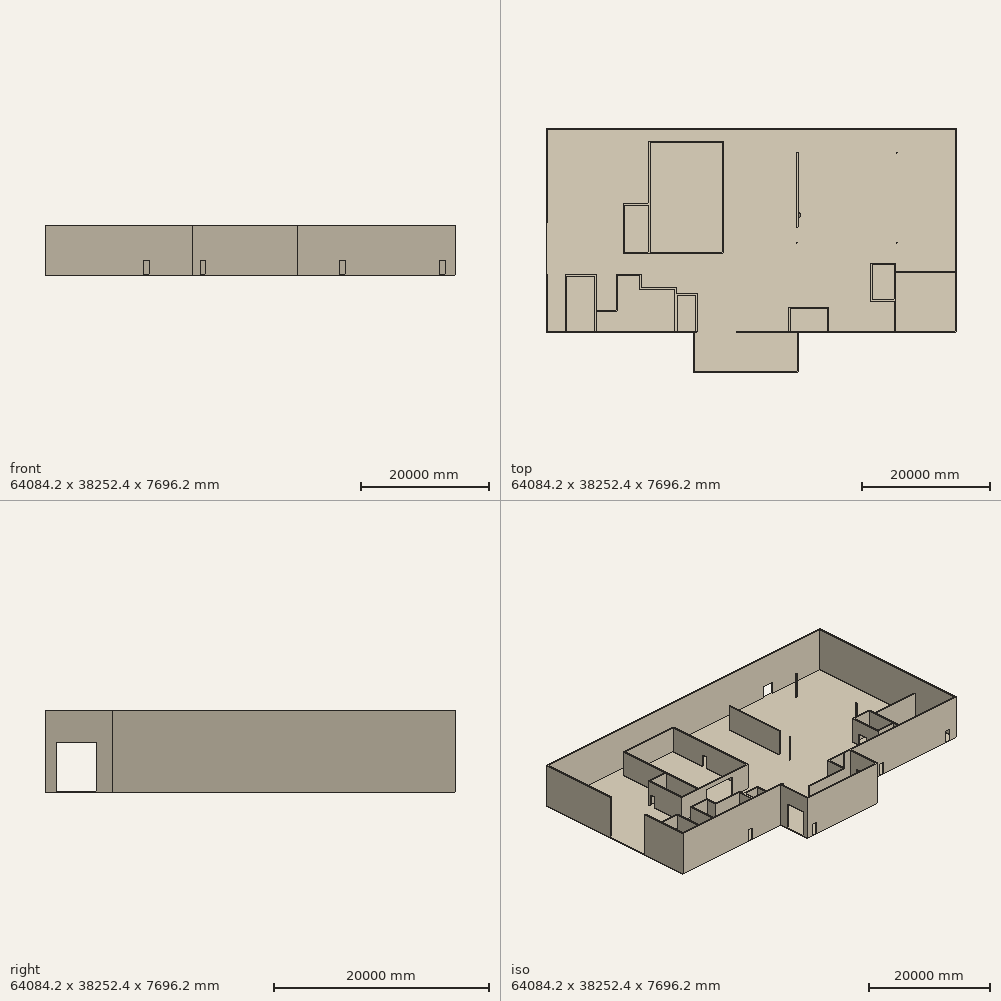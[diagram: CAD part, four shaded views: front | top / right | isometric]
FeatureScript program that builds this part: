
annotation { "Feature Type Name" : "Feature", "Feature Type Description" : "" }
export const myFeature = defineFeature(function(context is Context, id is Id, definition is map)
    precondition{}
    {
        {
            var Q0;
            Q0=qCreatedBy(makeId("Top.planeOp"),FACE);
            var sketch = newSketch(context, id + "F0", { "sketchPlane" : qUnion([Q0])});
            skLineSegment(sketch, "E0.bottom", {"start": v(-27660.6, 28059.69) * mm, "end": v(36423.6, 28059.69) * mm});
            skLineSegment(sketch, "E0.top", {"start": v(-27660.6, -3944.31) * mm, "end": v(36423.6, -3944.31) * mm});
            skLineSegment(sketch, "E0.left", {"start": v(-27660.6, 28059.69) * mm, "end": v(-27660.6, -3944.31) * mm});
            skLineSegment(sketch, "E0.right", {"start": v(36423.6, 28059.69) * mm, "end": v(36423.6, -3944.31) * mm});
            skLineSegment(sketch, "E1.bottom", {"start": v(-11658.6, 26002.29) * mm, "end": v(0, 26002.29) * mm});
            skLineSegment(sketch, "E1.top", {"start": v(-11658.6, 8400.09) * mm, "end": v(0, 8400.09) * mm});
            skLineSegment(sketch, "E1.left", {"start": v(-11658.6, 26002.29) * mm, "end": v(-11658.6, 8400.09) * mm});
            skLineSegment(sketch, "E1.right", {"start": v(0, 26002.29) * mm, "end": v(0, 8400.09) * mm});
            skLineSegment(sketch, "E2.bottom", {"start": v(-15621, 16248.69) * mm, "end": v(-11658.6, 16248.69) * mm});
            skLineSegment(sketch, "E2.top", {"start": v(-15621, 8400.09) * mm, "end": v(-11658.6, 8400.09) * mm});
            skLineSegment(sketch, "E2.left", {"start": v(-15621, 16248.69) * mm, "end": v(-15621, 8400.09) * mm});
            skLineSegment(sketch, "E2.right", {"start": v(-11658.6, 16248.69) * mm, "end": v(-11658.6, 8400.09) * mm});
            skLineSegment(sketch, "E3.bottom", {"start": v(-24765, 5123.49) * mm, "end": v(-19888.2, 5123.49) * mm});
            skLineSegment(sketch, "E3.left", {"start": v(-24765, 5123.49) * mm, "end": v(-24765, -3715.71) * mm});
            skLineSegment(sketch, "E3.right", {"start": v(-19888.2, 5123.49) * mm, "end": v(-19888.2, -3715.71) * mm});
            skLineSegment(sketch, "E4", {"start": v(-19888.2, -439.11) * mm, "end": v(-16764, -439.11) * mm});
            skLineSegment(sketch, "E5", {"start": v(-16764, -439.11) * mm, "end": v(-16764, 5199.69) * mm});
            skLineSegment(sketch, "E6", {"start": v(-16764, 5199.69) * mm, "end": v(-12877.8, 5199.69) * mm});
            skLineSegment(sketch, "E7", {"start": v(-12877.8, 5199.69) * mm, "end": v(-12877.8, 3142.29) * mm});
            skLineSegment(sketch, "E8", {"start": v(-12877.8, 3142.29) * mm, "end": v(-7391.4, 3142.29) * mm});
            skLineSegment(sketch, "E9.bottom", {"start": v(-4114.8, 2151.69) * mm, "end": v(-7391.4, 2151.69) * mm});
            skLineSegment(sketch, "E9.top", {"start": v(-4114.8, -3944.31) * mm, "end": v(-4724.4, -3944.31) * mm});
            skLineSegment(sketch, "E9.left", {"start": v(-4114.8, 2151.69) * mm, "end": v(-4114.8, -3715.71) * mm});
            skLineSegment(sketch, "E10.bottom", {"start": v(10210.8, 94.29) * mm, "end": v(16459.2, 94.29) * mm});
            skLineSegment(sketch, "E10.top", {"start": v(10210.8, -3715.71) * mm, "end": v(16459.2, -3715.71) * mm});
            skLineSegment(sketch, "E10.left", {"start": v(10210.8, 94.29) * mm, "end": v(10210.8, -3715.71) * mm});
            skLineSegment(sketch, "E10.right", {"start": v(16459.2, 94.29) * mm, "end": v(16459.2, -3715.71) * mm});
            skLineSegment(sketch, "E11.bottom", {"start": v(23012.4, 6952.29) * mm, "end": v(26898.6, 6952.29) * mm});
            skLineSegment(sketch, "E11.top", {"start": v(23012.4, 1008.69) * mm, "end": v(26670, 1008.69) * mm});
            skLineSegment(sketch, "E11.left", {"start": v(23012.4, 6952.29) * mm, "end": v(23012.4, 1008.69) * mm});
            skLineSegment(sketch, "E12.bottom", {"start": v(26898.6, 5428.29) * mm, "end": v(36195, 5428.29) * mm});
            skLineSegment(sketch, "E12.left", {"start": v(26898.6, 5428.29) * mm, "end": v(26898.6, -3715.71) * mm});
            skLineSegment(sketch, "E13", {"start": v(11430, 24325.89) * mm, "end": v(11430, 12591.09) * mm});
            skLineSegment(sketch, "E14", {"start": v(-24765, 5123.49) * mm, "end": v(-27432, 5123.49) * mm, "construction": true});
            skLineSegment(sketch, "E15", {"start": v(-24765, 4056.69) * mm, "end": v(-24536.4, 4056.69) * mm});
            skLineSegment(sketch, "E16", {"start": v(-24765, 3142.29) * mm, "end": v(-24536.4, 3142.29) * mm});
            skLineSegment(sketch, "E17", {"start": v(-21259.8, 5123.49) * mm, "end": v(-21259.8, 4894.89) * mm});
            skLineSegment(sketch, "E18", {"start": v(-20345.4, 5123.49) * mm, "end": v(-20345.4, 4894.89) * mm});
            skLineSegment(sketch, "E19", {"start": v(-12725.4, 3142.29) * mm, "end": v(-12725.4, 2913.69) * mm});
            skLineSegment(sketch, "E20", {"start": v(-10744.2, 3142.29) * mm, "end": v(-10744.2, 2913.69) * mm});
            skLineSegment(sketch, "E21", {"start": v(-4343.4, -2039.31) * mm, "end": v(-4114.8, -2039.31) * mm});
            skLineSegment(sketch, "E22", {"start": v(-4343.4, -2953.71) * mm, "end": v(-4114.8, -2953.71) * mm});
            skLineSegment(sketch, "E23", {"start": v(10591.8, 94.29) * mm, "end": v(10591.8, -134.31) * mm});
            skLineSegment(sketch, "E24", {"start": v(11506.2, 94.29) * mm, "end": v(11506.2, -134.31) * mm});
            skLineSegment(sketch, "E25", {"start": v(18288, -3715.71) * mm, "end": v(18288, -3944.31) * mm});
            skLineSegment(sketch, "E26", {"start": v(19202.4, -3715.71) * mm, "end": v(19202.4, -3944.31) * mm});
            skLineSegment(sketch, "E27.bottom", {"start": v(-4724.4, -3944.31) * mm, "end": v(11734.8, -3944.31) * mm});
            skLineSegment(sketch, "E27.top", {"start": v(-4724.4, -10192.71) * mm, "end": v(11734.8, -10192.71) * mm});
            skLineSegment(sketch, "E27.left", {"start": v(-4724.4, -3944.31) * mm, "end": v(-4724.4, -10192.71) * mm});
            skLineSegment(sketch, "E27.right", {"start": v(11734.8, -3944.31) * mm, "end": v(11734.8, -10192.71) * mm});
            skLineSegment(sketch, "E28", {"start": v(23241, 5580.69) * mm, "end": v(23012.4, 5580.69) * mm});
            skLineSegment(sketch, "E29", {"start": v(23241, 3675.69) * mm, "end": v(23012.4, 3675.69) * mm});
            skLineSegment(sketch, "E30", {"start": v(27432, 5656.89) * mm, "end": v(27432, 5428.29) * mm});
            skLineSegment(sketch, "E31", {"start": v(29413.2, 5656.89) * mm, "end": v(29413.2, 5428.29) * mm});
            skLineSegment(sketch, "E32", {"start": v(23012.4, 28059.69) * mm, "end": v(23012.4, 27831.09) * mm});
            skLineSegment(sketch, "E33", {"start": v(25146, 27831.09) * mm, "end": v(25146, 28059.69) * mm});
            skLineSegment(sketch, "E34", {"start": v(-914.4, 27831.09) * mm, "end": v(-914.4, 28059.69) * mm});
            skLineSegment(sketch, "E35", {"start": v(1600.2, 27831.09) * mm, "end": v(1600.2, 28059.69) * mm});
            skLineSegment(sketch, "E36", {"start": v(-26136.6, 27831.09) * mm, "end": v(-26136.6, 28059.69) * mm});
            skLineSegment(sketch, "E37", {"start": v(-24003, 27831.09) * mm, "end": v(-24003, 28059.69) * mm});
            skLineSegment(sketch, "E38", {"start": v(-15621, 15791.49) * mm, "end": v(-15392.4, 15791.49) * mm});
            skLineSegment(sketch, "E39", {"start": v(-15621, 14877.09) * mm, "end": v(-15392.4, 14877.09) * mm});
            skLineSegment(sketch, "E40", {"start": v(-228.6, 18839.49) * mm, "end": v(0, 18839.49) * mm});
            skLineSegment(sketch, "E41", {"start": v(-228.6, 17925.09) * mm, "end": v(0, 17925.09) * mm});
            skLineSegment(sketch, "E42", {"start": v(-12344.4, -3715.71) * mm, "end": v(-12344.4, -3944.31) * mm});
            skLineSegment(sketch, "E43", {"start": v(-11430, -3715.71) * mm, "end": v(-11430, -3944.31) * mm});
            skLineSegment(sketch, "E44", {"start": v(33909, -3715.71) * mm, "end": v(33909, -3944.31) * mm});
            skLineSegment(sketch, "E45", {"start": v(34899.6, -3715.71) * mm, "end": v(34899.6, -3944.31) * mm});
            skLineSegment(sketch, "E46.0", {"start": v(-27432, 27831.09) * mm, "end": v(36195, 27831.09) * mm});
            skLineSegment(sketch, "E46.1", {"start": v(-27432, 27831.09) * mm, "end": v(-27432, -3715.71) * mm});
            skLineSegment(sketch, "E46.2", {"start": v(-27432, -3715.71) * mm, "end": v(36195, -3715.71) * mm});
            skLineSegment(sketch, "E46.3", {"start": v(36195, 27831.09) * mm, "end": v(36195, -3715.71) * mm});
            skLineSegment(sketch, "E47.0", {"start": v(26670, 5656.89) * mm, "end": v(36195, 5656.89) * mm});
            skLineSegment(sketch, "E47.1", {"start": v(26670, 5656.89) * mm, "end": v(26670, -3715.71) * mm});
            skLineSegment(sketch, "E48", {"start": v(26898.6, 5656.89) * mm, "end": v(26898.6, 6952.29) * mm});
            skLineSegment(sketch, "E49.0", {"start": v(23241, 1237.29) * mm, "end": v(26670, 1237.29) * mm});
            skLineSegment(sketch, "E49.1", {"start": v(23241, 6723.69) * mm, "end": v(23241, 1237.29) * mm});
            skLineSegment(sketch, "E49.2", {"start": v(23241, 6723.69) * mm, "end": v(26670, 6723.69) * mm});
            skLineSegment(sketch, "E49.3", {"start": v(26670, 5656.89) * mm, "end": v(26670, 6723.69) * mm});
            skLineSegment(sketch, "E50.0", {"start": v(10439.4, -134.31) * mm, "end": v(10439.4, -3715.71) * mm});
            skLineSegment(sketch, "E50.1", {"start": v(10439.4, -134.31) * mm, "end": v(16230.6, -134.31) * mm});
            skLineSegment(sketch, "E50.2", {"start": v(16230.6, -134.31) * mm, "end": v(16230.6, -3715.71) * mm});
            skLineSegment(sketch, "E51.0", {"start": v(11506.2, -3944.31) * mm, "end": v(11506.2, -9964.11) * mm});
            skLineSegment(sketch, "E51.1", {"start": v(-4495.8, -9964.11) * mm, "end": v(11506.2, -9964.11) * mm});
            skLineSegment(sketch, "E51.2", {"start": v(-4495.8, -3944.31) * mm, "end": v(-4495.8, -9964.11) * mm});
            skLineSegment(sketch, "E52", {"start": v(-7391.4, -3715.71) * mm, "end": v(-7391.4, 3142.29) * mm});
            skLineSegment(sketch, "E53.0", {"start": v(-4343.4, 1923.09) * mm, "end": v(-7162.8, 1923.09) * mm});
            skLineSegment(sketch, "E53.1", {"start": v(-4343.4, 1923.09) * mm, "end": v(-4343.4, -3715.71) * mm});
            skLineSegment(sketch, "E54", {"start": v(-7162.8, 1923.09) * mm, "end": v(-7162.8, -3715.71) * mm});
            skLineSegment(sketch, "E55.0", {"start": v(-7620, -3715.71) * mm, "end": v(-7620, 2913.69) * mm});
            skLineSegment(sketch, "E55.1", {"start": v(-13106.4, 2913.69) * mm, "end": v(-7620, 2913.69) * mm});
            skLineSegment(sketch, "E55.2", {"start": v(-19888.2, -667.71) * mm, "end": v(-16535.4, -667.71) * mm});
            skLineSegment(sketch, "E55.3", {"start": v(-16535.4, -667.71) * mm, "end": v(-16535.4, 4971.09) * mm});
            skLineSegment(sketch, "E55.4", {"start": v(-16535.4, 4971.09) * mm, "end": v(-13106.4, 4971.09) * mm});
            skLineSegment(sketch, "E55.5", {"start": v(-13106.4, 4971.09) * mm, "end": v(-13106.4, 2913.69) * mm});
            skLineSegment(sketch, "E56.0", {"start": v(-24536.4, 4894.89) * mm, "end": v(-24536.4, -3715.71) * mm});
            skLineSegment(sketch, "E56.1", {"start": v(-24536.4, 4894.89) * mm, "end": v(-20116.8, 4894.89) * mm});
            skLineSegment(sketch, "E56.2", {"start": v(-20116.8, 4894.89) * mm, "end": v(-20116.8, -3715.71) * mm});
            skLineSegment(sketch, "E57.0", {"start": v(-15392.4, 16020.09) * mm, "end": v(-11658.6, 16020.09) * mm});
            skLineSegment(sketch, "E57.1", {"start": v(-15392.4, 16020.09) * mm, "end": v(-15392.4, 8628.69) * mm});
            skLineSegment(sketch, "E57.2", {"start": v(-15392.4, 8628.69) * mm, "end": v(-11658.6, 8628.69) * mm});
            skLineSegment(sketch, "E58.0", {"start": v(-11430, 25773.69) * mm, "end": v(-11430, 8628.69) * mm});
            skLineSegment(sketch, "E58.1", {"start": v(-11430, 25773.69) * mm, "end": v(-228.6, 25773.69) * mm});
            skLineSegment(sketch, "E58.2", {"start": v(-228.6, 25773.69) * mm, "end": v(-228.6, 8628.69) * mm});
            skLineSegment(sketch, "E58.3", {"start": v(-11430, 8628.69) * mm, "end": v(-228.6, 8628.69) * mm});
            skLineSegment(sketch, "E59", {"start": v(11430, 24325.89) * mm, "end": v(11658.6, 24325.89) * mm});
            skLineSegment(sketch, "E60", {"start": v(11658.6, 24325.89) * mm, "end": v(11658.6, 12591.09) * mm});
            skLineSegment(sketch, "E61", {"start": v(11658.6, 12591.09) * mm, "end": v(11430, 12591.09) * mm});
            skPoint(sketch, "E62", {"position": v(-27432, 13124.49) * mm});
            skPoint(sketch, "E63", {"position": v(-27660.6, 13124.49) * mm});
            skLineSegment(sketch, "E64", {"start": v(-27660.6, 5123.49) * mm, "end": v(-27660.6, -3944.31) * mm});
            skLineSegment(sketch, "E65", {"start": v(-27432, 5123.49) * mm, "end": v(-27432, -3715.71) * mm});
            skLineSegment(sketch, "E66", {"start": v(-27660.6, 13124.49) * mm, "end": v(-27660.6, 28059.69) * mm});
            skLineSegment(sketch, "E67", {"start": v(-27432, 27831.09) * mm, "end": v(-27432, 13124.49) * mm});
            skLineSegment(sketch, "E68", {"start": v(-27432, 5123.49) * mm, "end": v(-27660.6, 5123.49) * mm});
            skLineSegment(sketch, "E69", {"start": v(-27432, 13124.49) * mm, "end": v(-27660.6, 13124.49) * mm});
            skLineSegment(sketch, "E70.bottom", {"start": v(11353.8, 10152.69) * mm, "end": v(11506.2, 10152.69) * mm});
            skLineSegment(sketch, "E70.top", {"start": v(11353.8, 10000.29) * mm, "end": v(11506.2, 10000.29) * mm});
            skLineSegment(sketch, "E70.left", {"start": v(11353.8, 10152.69) * mm, "end": v(11353.8, 10000.29) * mm});
            skLineSegment(sketch, "E70.right", {"start": v(11506.2, 10152.69) * mm, "end": v(11506.2, 10000.29) * mm});
            skLineSegment(sketch, "E71", {"start": v(10210.8, -3715.71) * mm, "end": v(10210.8, -3944.31) * mm});
            skLineSegment(sketch, "E72", {"start": v(-4114.8, -3715.71) * mm, "end": v(-4114.8, -3944.31) * mm});
            skLineSegment(sketch, "E73", {"start": v(-4724.4, -5468.31) * mm, "end": v(-4495.8, -5468.31) * mm});
            skLineSegment(sketch, "E74", {"start": v(-4724.4, -9125.91) * mm, "end": v(-4495.8, -9125.91) * mm});
            skLineSegment(sketch, "E75", {"start": v(11506.2, -5468.31) * mm, "end": v(11734.8, -5468.31) * mm});
            skLineSegment(sketch, "E76", {"start": v(11506.2, -9125.91) * mm, "end": v(11734.8, -9125.91) * mm});
            skLineSegment(sketch, "E77", {"start": v(-3505.2, -9964.11) * mm, "end": v(-3505.2, -10192.71) * mm});
            skLineSegment(sketch, "E78", {"start": v(-2590.8, -9964.11) * mm, "end": v(-2590.8, -10192.71) * mm});
            skLineSegment(sketch, "E79.bottom", {"start": v(26974.8, 24249.69) * mm, "end": v(27127.2, 24249.69) * mm});
            skLineSegment(sketch, "E79.top", {"start": v(26974.8, 24097.29) * mm, "end": v(27127.2, 24097.29) * mm});
            skLineSegment(sketch, "E79.left", {"start": v(26974.8, 24249.69) * mm, "end": v(26974.8, 24097.29) * mm});
            skLineSegment(sketch, "E79.right", {"start": v(27127.2, 24249.69) * mm, "end": v(27127.2, 24097.29) * mm});
            skLineSegment(sketch, "E80.bottom", {"start": v(26974.8, 10228.89) * mm, "end": v(27127.2, 10228.89) * mm});
            skLineSegment(sketch, "E80.top", {"start": v(26974.8, 10076.49) * mm, "end": v(27127.2, 10076.49) * mm});
            skLineSegment(sketch, "E80.left", {"start": v(26974.8, 10228.89) * mm, "end": v(26974.8, 10076.49) * mm});
            skLineSegment(sketch, "E80.right", {"start": v(27127.2, 10228.89) * mm, "end": v(27127.2, 10076.49) * mm});
            skLineSegment(sketch, "E81.bottom", {"start": v(1981.2, -3715.71) * mm, "end": v(9906, -3715.71) * mm});
            skLineSegment(sketch, "E81.top", {"start": v(1981.2, 1465.89) * mm, "end": v(9906, 1465.89) * mm});
            skLineSegment(sketch, "E81.left", {"start": v(1981.2, -3715.71) * mm, "end": v(1981.2, 1465.89) * mm});
            skLineSegment(sketch, "E81.right", {"start": v(9906, -3715.71) * mm, "end": v(9906, 1465.89) * mm});
            skLineSegment(sketch, "E82.0", {"start": v(9677.4, -3715.71) * mm, "end": v(9677.4, 1237.29) * mm});
            skLineSegment(sketch, "E82.1", {"start": v(2209.8, 1237.29) * mm, "end": v(9677.4, 1237.29) * mm});
            skLineSegment(sketch, "E82.2", {"start": v(2209.8, -3715.71) * mm, "end": v(2209.8, 1237.29) * mm});
            skLineSegment(sketch, "E83", {"start": v(1981.2, 1084.89) * mm, "end": v(2209.8, 1084.89) * mm});
            skLineSegment(sketch, "E84", {"start": v(1981.2, 170.49) * mm, "end": v(2209.8, 170.49) * mm});
            skLineSegment(sketch, "E85", {"start": v(9677.4, 1084.89) * mm, "end": v(9906, 1084.89) * mm});
            skLineSegment(sketch, "E86", {"start": v(9677.4, 170.49) * mm, "end": v(9906, 170.49) * mm});
            skLineSegment(sketch, "E87", {"start": v(1981.2, -3715.71) * mm, "end": v(1981.2, -3944.31) * mm});
            skSolve(sketch);
        }
        {
            var Q0;
            Q0=qCreatedBy(makeId("Top.planeOp"),FACE);
            var sketch = newSketch(context, id + "F1", { "sketchPlane" : qUnion([Q0])});
            skLineSegment(sketch, "E88.0", {"start": v(-27660.6, 28059.69) * mm, "end": v(36423.6, 28059.69) * mm});
            skLineSegment(sketch, "E89.0", {"start": v(-27660.6, 28059.69) * mm, "end": v(-27660.6, -3944.31) * mm});
            skLineSegment(sketch, "E90.0", {"start": v(-27660.6, -3944.31) * mm, "end": v(36423.6, -3944.31) * mm});
            skLineSegment(sketch, "E91.0", {"start": v(36423.6, 28059.69) * mm, "end": v(36423.6, -3944.31) * mm});
            skPoint(sketch, "E92.0", {"position": v(-4724.4, -7068.51) * mm});
            skLineSegment(sketch, "E93.0", {"start": v(-4724.4, -3944.31) * mm, "end": v(-4724.4, -10192.71) * mm});
            skLineSegment(sketch, "E94.0", {"start": v(-4724.4, -10192.71) * mm, "end": v(11734.8, -10192.71) * mm});
            skLineSegment(sketch, "E95.0", {"start": v(11734.8, -3944.31) * mm, "end": v(11734.8, -10192.71) * mm});
            skSolve(sketch);
        }
        {
            var Q0;
            Q0 = qSketchRegion(id + "F1", true);
            extrude(context, id + "F2", {"entities" : qUnion([Q0]), "oppositeDirection" : true, "depth" : 76.2 * mm, "offsetDistance" : 30.48 * mm});
        }
        {
            var Q0;
            {var subQ1=sQuery(id+"F0.wireOp",EDGE,"E36");Q0=makeQuery(id+"F0.imprint","IMPRINT",FACE,{"disambiguationData":[TD([[makeQuery(id+"F0.imprint","IMPRINT",EDGE,{"derivedFrom":subQ1}),1.0]])]});}
            var Q1;
            {var subQ2=sQuery(id+"F0.wireOp",EDGE,"E34");Q1=makeQuery(id+"F0.imprint","IMPRINT",FACE,{"disambiguationData":[TD([[makeQuery(id+"F0.imprint","IMPRINT",EDGE,{"derivedFrom":subQ2}),1.0]])]});}
            var Q2;
            {var subQ0=sQuery(id+"F0.wireOp",EDGE,"E32");Q2=makeQuery(id+"F0.imprint","IMPRINT",FACE,{"disambiguationData":[TD([[makeQuery(id+"F0.imprint","IMPRINT",EDGE,{"derivedFrom":subQ0}),-1.0]])]});}
            var Q3;
            {var subQ0=sQuery(id+"F0.wireOp",EDGE,"E0.right");Q3=makeQuery(id+"F0.imprint","IMPRINT",FACE,{"disambiguationData":[TD([[makeQuery(id+"F0.imprint","IMPRINT",EDGE,{"derivedFrom":subQ0}),-1.0]])]});}
            var Q4;
            {var subQ1=sQuery(id+"F0.wireOp",EDGE,"E26");Q4=makeQuery(id+"F0.imprint","IMPRINT",FACE,{"disambiguationData":[TD([[makeQuery(id+"F0.imprint","IMPRINT",EDGE,{"derivedFrom":subQ1}),1.0]])]});}
            var Q5;
            {var subQ9=sQuery(id+"F0.wireOp",EDGE,"E25");Q5=makeQuery(id+"F0.imprint","IMPRINT",FACE,{"disambiguationData":[TD([[makeQuery(id+"F0.imprint","IMPRINT",EDGE,{"derivedFrom":subQ9}),-1.0]])]});}
            var Q6;
            {var subQ5=sQuery(id+"F0.wireOp",EDGE,"E75");Q6=makeQuery(id+"F0.imprint","IMPRINT",FACE,{"disambiguationData":[TD([[makeQuery(id+"F0.imprint","IMPRINT",EDGE,{"derivedFrom":subQ5}),1.0]])]});}
            var Q7;
            {var subQ3=sQuery(id+"F0.wireOp",EDGE,"E76");Q7=makeQuery(id+"F0.imprint","IMPRINT",FACE,{"disambiguationData":[TD([[makeQuery(id+"F0.imprint","IMPRINT",EDGE,{"derivedFrom":subQ3}),-1.0]])]});}
            var Q8;
            {var subQ3=sQuery(id+"F0.wireOp",EDGE,"E74");Q8=makeQuery(id+"F0.imprint","IMPRINT",FACE,{"disambiguationData":[TD([[makeQuery(id+"F0.imprint","IMPRINT",EDGE,{"derivedFrom":subQ3}),-1.0]])]});}
            var Q9;
            {var subQ5=sQuery(id+"F0.wireOp",EDGE,"E73");Q9=makeQuery(id+"F0.imprint","IMPRINT",FACE,{"disambiguationData":[TD([[makeQuery(id+"F0.imprint","IMPRINT",EDGE,{"derivedFrom":subQ5}),1.0]])]});}
            var Q10;
            {var subQ3=sQuery(id+"F0.wireOp",EDGE,"E43");Q10=makeQuery(id+"F0.imprint","IMPRINT",FACE,{"disambiguationData":[TD([[makeQuery(id+"F0.imprint","IMPRINT",EDGE,{"derivedFrom":subQ3}),1.0]])]});}
            var Q11;
            {var subQ4=sQuery(id+"F0.wireOp",EDGE,"E42");Q11=makeQuery(id+"F0.imprint","IMPRINT",FACE,{"disambiguationData":[TD([[makeQuery(id+"F0.imprint","IMPRINT",EDGE,{"derivedFrom":subQ4}),-1.0]])]});}
            var Q12;
            {var subQ0=sQuery(id+"F0.wireOp",EDGE,"E42");Q12=makeQuery(id+"F0.imprint","IMPRINT",FACE,{"disambiguationData":[TD([[makeQuery(id+"F0.imprint","IMPRINT",EDGE,{"derivedFrom":subQ0}),1.0]])]});}
            var Q13;
            {var subQ0=sQuery(id+"F0.wireOp",EDGE,"E73");Q13=makeQuery(id+"F0.imprint","IMPRINT",FACE,{"disambiguationData":[TD([[makeQuery(id+"F0.imprint","IMPRINT",EDGE,{"derivedFrom":subQ0}),-1.0]])]});}
            var Q14;
            {var subQ2=sQuery(id+"F0.wireOp",EDGE,"E77");Q14=makeQuery(id+"F0.imprint","IMPRINT",FACE,{"disambiguationData":[TD([[makeQuery(id+"F0.imprint","IMPRINT",EDGE,{"derivedFrom":subQ2}),1.0]])]});}
            var Q15;
            {var subQ0=sQuery(id+"F0.wireOp",EDGE,"E75");Q15=makeQuery(id+"F0.imprint","IMPRINT",FACE,{"disambiguationData":[TD([[makeQuery(id+"F0.imprint","IMPRINT",EDGE,{"derivedFrom":subQ0}),-1.0]])]});}
            var Q16;
            {var subQ0=sQuery(id+"F0.wireOp",EDGE,"E25");Q16=makeQuery(id+"F0.imprint","IMPRINT",FACE,{"disambiguationData":[TD([[makeQuery(id+"F0.imprint","IMPRINT",EDGE,{"derivedFrom":subQ0}),1.0]])]});}
            var Q17;
            {var subQ0=sQuery(id+"F0.wireOp",EDGE,"E44");Q17=makeQuery(id+"F0.imprint","IMPRINT",FACE,{"disambiguationData":[TD([[makeQuery(id+"F0.imprint","IMPRINT",EDGE,{"derivedFrom":subQ0}),1.0]])]});}
            var Q18;
            {var subQ0=sQuery(id+"F0.wireOp",EDGE,"E32");Q18=makeQuery(id+"F0.imprint","IMPRINT",FACE,{"disambiguationData":[TD([[makeQuery(id+"F0.imprint","IMPRINT",EDGE,{"derivedFrom":subQ0}),1.0]])]});}
            var Q19;
            {var subQ0=sQuery(id+"F0.wireOp",EDGE,"E34");Q19=makeQuery(id+"F0.imprint","IMPRINT",FACE,{"disambiguationData":[TD([[makeQuery(id+"F0.imprint","IMPRINT",EDGE,{"derivedFrom":subQ0}),-1.0]])]});}
            var Q20;
            {var subQ2=sQuery(id+"F0.wireOp",EDGE,"E36");Q20=makeQuery(id+"F0.imprint","IMPRINT",FACE,{"disambiguationData":[TD([[makeQuery(id+"F0.imprint","IMPRINT",EDGE,{"derivedFrom":subQ2}),-1.0]])]});}
            extrude(context, id + "F3", {"entities" : qUnion([Q0, Q1, Q2, Q3, Q4, Q5, Q6, Q7, Q8, Q9, Q10, Q11, Q12, Q13, Q14, Q15, Q16, Q17, Q18, Q19, Q20]), "operationType" : NewBodyOperationType.ADD, "depth" : 7620 * mm, "offsetDistance" : 30.48 * mm});
        }
        {
            var Q0;
            {var subQ0=sQuery(id+"F0.wireOp",EDGE,"E42");Q0=makeQuery(id+"F0.imprint","IMPRINT",FACE,{"disambiguationData":[TD([[makeQuery(id+"F0.imprint","IMPRINT",EDGE,{"derivedFrom":subQ0}),1.0]])]});}
            var Q1;
            {var subQ2=sQuery(id+"F0.wireOp",EDGE,"E77");Q1=makeQuery(id+"F0.imprint","IMPRINT",FACE,{"disambiguationData":[TD([[makeQuery(id+"F0.imprint","IMPRINT",EDGE,{"derivedFrom":subQ2}),1.0]])]});}
            var Q2;
            {var subQ0=sQuery(id+"F0.wireOp",EDGE,"E25");Q2=makeQuery(id+"F0.imprint","IMPRINT",FACE,{"disambiguationData":[TD([[makeQuery(id+"F0.imprint","IMPRINT",EDGE,{"derivedFrom":subQ0}),1.0]])]});}
            var Q3;
            {var subQ0=sQuery(id+"F0.wireOp",EDGE,"E44");Q3=makeQuery(id+"F0.imprint","IMPRINT",FACE,{"disambiguationData":[TD([[makeQuery(id+"F0.imprint","IMPRINT",EDGE,{"derivedFrom":subQ0}),1.0]])]});}
            var Q4;
            {var subQ0=sQuery(id+"F0.wireOp",EDGE,"E32");Q4=makeQuery(id+"F0.imprint","IMPRINT",FACE,{"disambiguationData":[TD([[makeQuery(id+"F0.imprint","IMPRINT",EDGE,{"derivedFrom":subQ0}),1.0]])]});}
            var Q5;
            {var subQ0=sQuery(id+"F0.wireOp",EDGE,"E34");Q5=makeQuery(id+"F0.imprint","IMPRINT",FACE,{"disambiguationData":[TD([[makeQuery(id+"F0.imprint","IMPRINT",EDGE,{"derivedFrom":subQ0}),-1.0]])]});}
            var Q6;
            {var subQ2=sQuery(id+"F0.wireOp",EDGE,"E36");Q6=makeQuery(id+"F0.imprint","IMPRINT",FACE,{"disambiguationData":[TD([[makeQuery(id+"F0.imprint","IMPRINT",EDGE,{"derivedFrom":subQ2}),-1.0]])]});}
            extrude(context, id + "F4", {"entities" : qUnion([Q0, Q1, Q2, Q3, Q4, Q5, Q6]), "operationType" : NewBodyOperationType.REMOVE, "depth" : 2133.6 * mm, "offsetDistance" : 30.48 * mm});
        }
        {
            var Q0;
            {var subQ0=sQuery(id+"F0.wireOp",EDGE,"E73");Q0=makeQuery(id+"F0.imprint","IMPRINT",FACE,{"disambiguationData":[TD([[makeQuery(id+"F0.imprint","IMPRINT",EDGE,{"derivedFrom":subQ0}),-1.0]])]});}
            var Q1;
            {var subQ0=sQuery(id+"F0.wireOp",EDGE,"E75");Q1=makeQuery(id+"F0.imprint","IMPRINT",FACE,{"disambiguationData":[TD([[makeQuery(id+"F0.imprint","IMPRINT",EDGE,{"derivedFrom":subQ0}),-1.0]])]});}
            extrude(context, id + "F5", {"entities" : qUnion([Q0, Q1]), "operationType" : NewBodyOperationType.REMOVE, "depth" : 4572 * mm, "offsetDistance" : 30.48 * mm});
        }
        {
            var Q0;
            {var subQ0=sQuery(id+"F0.wireOp",EDGE,"E16");Q0=makeQuery(id+"F0.imprint","IMPRINT",FACE,{"disambiguationData":[TD([[makeQuery(id+"F0.imprint","IMPRINT",EDGE,{"derivedFrom":subQ0}),-1.0]])]});}
            var Q1;
            {var subQ2=sQuery(id+"F0.wireOp",EDGE,"E15");Q1=makeQuery(id+"F0.imprint","IMPRINT",FACE,{"disambiguationData":[TD([[makeQuery(id+"F0.imprint","IMPRINT",EDGE,{"derivedFrom":subQ2}),-1.0]])]});}
            var Q2;
            {var subQ0=sQuery(id+"F0.wireOp",EDGE,"E15");Q2=makeQuery(id+"F0.imprint","IMPRINT",FACE,{"disambiguationData":[TD([[makeQuery(id+"F0.imprint","IMPRINT",EDGE,{"derivedFrom":subQ0}),1.0]])]});}
            var Q3;
            {var subQ0=sQuery(id+"F0.wireOp",EDGE,"E17");Q3=makeQuery(id+"F0.imprint","IMPRINT",FACE,{"disambiguationData":[TD([[makeQuery(id+"F0.imprint","IMPRINT",EDGE,{"derivedFrom":subQ0}),1.0]])]});}
            var Q4;
            {var subQ3=sQuery(id+"F0.wireOp",EDGE,"E18");Q4=makeQuery(id+"F0.imprint","IMPRINT",FACE,{"disambiguationData":[TD([[makeQuery(id+"F0.imprint","IMPRINT",EDGE,{"derivedFrom":subQ3}),1.0]])]});}
            var Q5;
            {var subQ7=sQuery(id+"F0.wireOp",EDGE,"E4");Q5=makeQuery(id+"F0.imprint","IMPRINT",FACE,{"disambiguationData":[TD([[makeQuery(id+"F0.imprint","IMPRINT",EDGE,{"derivedFrom":subQ7}),-1.0]])]});}
            var Q6;
            {var subQ2=sQuery(id+"F0.wireOp",EDGE,"E19");Q6=makeQuery(id+"F0.imprint","IMPRINT",FACE,{"disambiguationData":[TD([[makeQuery(id+"F0.imprint","IMPRINT",EDGE,{"derivedFrom":subQ2}),1.0]])]});}
            var Q7;
            {var subQ5=sQuery(id+"F0.wireOp",EDGE,"E20");Q7=makeQuery(id+"F0.imprint","IMPRINT",FACE,{"disambiguationData":[TD([[makeQuery(id+"F0.imprint","IMPRINT",EDGE,{"derivedFrom":subQ5}),1.0]])]});}
            var Q8;
            {var subQ7=sQuery(id+"F0.wireOp",EDGE,"E9.bottom");Q8=makeQuery(id+"F0.imprint","IMPRINT",FACE,{"disambiguationData":[TD([[makeQuery(id+"F0.imprint","IMPRINT",EDGE,{"derivedFrom":subQ7}),1.0]])]});}
            var Q9;
            {var subQ0=sQuery(id+"F0.wireOp",EDGE,"E21");Q9=makeQuery(id+"F0.imprint","IMPRINT",FACE,{"disambiguationData":[TD([[makeQuery(id+"F0.imprint","IMPRINT",EDGE,{"derivedFrom":subQ0}),-1.0]])]});}
            var Q10;
            {var subQ3=sQuery(id+"F0.wireOp",EDGE,"E22");Q10=makeQuery(id+"F0.imprint","IMPRINT",FACE,{"disambiguationData":[TD([[makeQuery(id+"F0.imprint","IMPRINT",EDGE,{"derivedFrom":subQ3}),-1.0]])]});}
            var Q11;
            {var subQ1=sQuery(id+"F0.wireOp",EDGE,"E2.top");Q11=makeQuery(id+"F0.imprint","IMPRINT",FACE,{"disambiguationData":[TD([[makeQuery(id+"F0.imprint","IMPRINT",EDGE,{"derivedFrom":subQ1}),1.0]])]});}
            var Q12;
            {var subQ3=sQuery(id+"F0.wireOp",EDGE,"E1.bottom");Q12=makeQuery(id+"F0.imprint","IMPRINT",FACE,{"disambiguationData":[TD([[makeQuery(id+"F0.imprint","IMPRINT",EDGE,{"derivedFrom":subQ3}),-1.0]])]});}
            var Q13;
            {var subQ2=sQuery(id+"F0.wireOp",EDGE,"E38");Q13=makeQuery(id+"F0.imprint","IMPRINT",FACE,{"disambiguationData":[TD([[makeQuery(id+"F0.imprint","IMPRINT",EDGE,{"derivedFrom":subQ2}),-1.0]])]});}
            var Q14;
            {var subQ1=sQuery(id+"F0.wireOp",EDGE,"E10.left");Q14=makeQuery(id+"F0.imprint","IMPRINT",FACE,{"disambiguationData":[TD([[makeQuery(id+"F0.imprint","IMPRINT",EDGE,{"derivedFrom":subQ1}),1.0]])]});}
            var Q15;
            {var subQ2=sQuery(id+"F0.wireOp",EDGE,"E23");Q15=makeQuery(id+"F0.imprint","IMPRINT",FACE,{"disambiguationData":[TD([[makeQuery(id+"F0.imprint","IMPRINT",EDGE,{"derivedFrom":subQ2}),1.0]])]});}
            var Q16;
            {var subQ1=sQuery(id+"F0.wireOp",EDGE,"E10.right");Q16=makeQuery(id+"F0.imprint","IMPRINT",FACE,{"disambiguationData":[TD([[makeQuery(id+"F0.imprint","IMPRINT",EDGE,{"derivedFrom":subQ1}),-1.0]])]});}
            var Q17;
            {var subQ1=sQuery(id+"F0.wireOp",EDGE,"E12.left");Q17=makeQuery(id+"F0.imprint","IMPRINT",FACE,{"disambiguationData":[TD([[makeQuery(id+"F0.imprint","IMPRINT",EDGE,{"derivedFrom":subQ1}),-1.0]])]});}
            var Q18;
            {var subQ2=sQuery(id+"F0.wireOp",EDGE,"E28");Q18=makeQuery(id+"F0.imprint","IMPRINT",FACE,{"disambiguationData":[TD([[makeQuery(id+"F0.imprint","IMPRINT",EDGE,{"derivedFrom":subQ2}),1.0]])]});}
            var Q19;
            {var subQ3=sQuery(id+"F0.wireOp",EDGE,"E11.bottom");Q19=makeQuery(id+"F0.imprint","IMPRINT",FACE,{"disambiguationData":[TD([[makeQuery(id+"F0.imprint","IMPRINT",EDGE,{"derivedFrom":subQ3}),-1.0]])]});}
            var Q20;
            {var subQ2=sQuery(id+"F0.wireOp",EDGE,"E30");Q20=makeQuery(id+"F0.imprint","IMPRINT",FACE,{"disambiguationData":[TD([[makeQuery(id+"F0.imprint","IMPRINT",EDGE,{"derivedFrom":subQ2}),1.0]])]});}
            var Q21;
            {var subQ0=sQuery(id+"F0.wireOp",EDGE,"E31");Q21=makeQuery(id+"F0.imprint","IMPRINT",FACE,{"disambiguationData":[TD([[makeQuery(id+"F0.imprint","IMPRINT",EDGE,{"derivedFrom":subQ0}),1.0]])]});}
            var Q22;
            Q22=makeQuery(id+"F0.imprint","IMPRINT",FACE,{"disambiguationData":[TD([[makeQuery(id+"F0.imprint","IMPRINT",EDGE,{"derivedFrom":sQuery(id+"F0.wireOp",EDGE,"E13")}),1.0]])]});
            var Q23;
            {var subQ2=sQuery(id+"F0.wireOp",EDGE,"E11.top");Q23=makeQuery(id+"F0.imprint","IMPRINT",FACE,{"disambiguationData":[TD([[makeQuery(id+"F0.imprint","IMPRINT",EDGE,{"derivedFrom":subQ2}),1.0]])]});}
            var Q24;
            Q24=makeQuery(id+"F0.imprint","IMPRINT",FACE,{"disambiguationData":[TD([[makeQuery(id+"F0.imprint","IMPRINT",EDGE,{"derivedFrom":sQuery(id+"F0.wireOp",EDGE,"E70.bottom")}),-1.0]])]});
            var Q25;
            {var subQ2=sQuery(id+"F0.wireOp",EDGE,"E40");Q25=makeQuery(id+"F0.imprint","IMPRINT",FACE,{"disambiguationData":[TD([[makeQuery(id+"F0.imprint","IMPRINT",EDGE,{"derivedFrom":subQ2}),-1.0]])]});}
            var Q26;
            {var subQ2=sQuery(id+"F0.wireOp",EDGE,"E2.bottom");Q26=makeQuery(id+"F0.imprint","IMPRINT",FACE,{"disambiguationData":[TD([[makeQuery(id+"F0.imprint","IMPRINT",EDGE,{"derivedFrom":subQ2}),-1.0]])]});}
            var Q27;
            Q27=makeQuery(id+"F0.imprint","IMPRINT",FACE,{"disambiguationData":[TD([[makeQuery(id+"F0.imprint","IMPRINT",EDGE,{"derivedFrom":sQuery(id+"F0.wireOp",EDGE,"E80.bottom")}),-1.0]])]});
            var Q28;
            Q28=makeQuery(id+"F0.imprint","IMPRINT",FACE,{"disambiguationData":[TD([[makeQuery(id+"F0.imprint","IMPRINT",EDGE,{"derivedFrom":sQuery(id+"F0.wireOp",EDGE,"E79.bottom")}),-1.0]])]});
            var Q29;
            {var subQ3=sQuery(id+"F0.wireOp",EDGE,"E71");Q29=makeQuery(id+"F0.imprint","IMPRINT",FACE,{"disambiguationData":[TD([[makeQuery(id+"F0.imprint","IMPRINT",EDGE,{"derivedFrom":subQ3}),-1.0]])]});}
            extrude(context, id + "F6", {"entities" : qUnion([Q0, Q1, Q2, Q3, Q4, Q5, Q6, Q7, Q8, Q9, Q10, Q11, Q12, Q13, Q14, Q15, Q16, Q17, Q18, Q19, Q20, Q21, Q22, Q23, Q24, Q25, Q26, Q27, Q28, Q29]), "operationType" : NewBodyOperationType.ADD, "flatOperationType" : FlatOperationType.REMOVE, "depth" : 4572 * mm, "offsetDistance" : 30.48 * mm, "domain" : OperationDomain.MODEL});
        }
        {
            var Q0;
            {var subQ2=sQuery(id+"F0.wireOp",EDGE,"E15");Q0=makeQuery(id+"F0.imprint","IMPRINT",FACE,{"disambiguationData":[TD([[makeQuery(id+"F0.imprint","IMPRINT",EDGE,{"derivedFrom":subQ2}),-1.0]])]});}
            var Q1;
            {var subQ0=sQuery(id+"F0.wireOp",EDGE,"E17");Q1=makeQuery(id+"F0.imprint","IMPRINT",FACE,{"disambiguationData":[TD([[makeQuery(id+"F0.imprint","IMPRINT",EDGE,{"derivedFrom":subQ0}),1.0]])]});}
            var Q2;
            {var subQ2=sQuery(id+"F0.wireOp",EDGE,"E19");Q2=makeQuery(id+"F0.imprint","IMPRINT",FACE,{"disambiguationData":[TD([[makeQuery(id+"F0.imprint","IMPRINT",EDGE,{"derivedFrom":subQ2}),1.0]])]});}
            var Q3;
            {var subQ0=sQuery(id+"F0.wireOp",EDGE,"E21");Q3=makeQuery(id+"F0.imprint","IMPRINT",FACE,{"disambiguationData":[TD([[makeQuery(id+"F0.imprint","IMPRINT",EDGE,{"derivedFrom":subQ0}),-1.0]])]});}
            var Q4;
            {var subQ2=sQuery(id+"F0.wireOp",EDGE,"E38");Q4=makeQuery(id+"F0.imprint","IMPRINT",FACE,{"disambiguationData":[TD([[makeQuery(id+"F0.imprint","IMPRINT",EDGE,{"derivedFrom":subQ2}),-1.0]])]});}
            var Q5;
            {var subQ2=sQuery(id+"F0.wireOp",EDGE,"E40");Q5=makeQuery(id+"F0.imprint","IMPRINT",FACE,{"disambiguationData":[TD([[makeQuery(id+"F0.imprint","IMPRINT",EDGE,{"derivedFrom":subQ2}),-1.0]])]});}
            var Q6;
            {var subQ2=sQuery(id+"F0.wireOp",EDGE,"E23");Q6=makeQuery(id+"F0.imprint","IMPRINT",FACE,{"disambiguationData":[TD([[makeQuery(id+"F0.imprint","IMPRINT",EDGE,{"derivedFrom":subQ2}),1.0]])]});}
            var Q7;
            {var subQ2=sQuery(id+"F0.wireOp",EDGE,"E28");Q7=makeQuery(id+"F0.imprint","IMPRINT",FACE,{"disambiguationData":[TD([[makeQuery(id+"F0.imprint","IMPRINT",EDGE,{"derivedFrom":subQ2}),1.0]])]});}
            var Q8;
            {var subQ2=sQuery(id+"F0.wireOp",EDGE,"E30");Q8=makeQuery(id+"F0.imprint","IMPRINT",FACE,{"disambiguationData":[TD([[makeQuery(id+"F0.imprint","IMPRINT",EDGE,{"derivedFrom":subQ2}),1.0]])]});}
            var Q9;
            {var subQ0=sQuery(id+"F0.wireOp",EDGE,"E83");Q9=makeQuery(id+"F0.imprint","IMPRINT",FACE,{"disambiguationData":[TD([[makeQuery(id+"F0.imprint","IMPRINT",EDGE,{"derivedFrom":subQ0}),-1.0]])]});}
            var Q10;
            {var subQ0=sQuery(id+"F0.wireOp",EDGE,"E85");Q10=makeQuery(id+"F0.imprint","IMPRINT",FACE,{"disambiguationData":[TD([[makeQuery(id+"F0.imprint","IMPRINT",EDGE,{"derivedFrom":subQ0}),-1.0]])]});}
            extrude(context, id + "F7", {"entities" : qUnion([Q0, Q1, Q2, Q3, Q4, Q5, Q6, Q7, Q8, Q9, Q10]), "operationType" : NewBodyOperationType.REMOVE, "depth" : 2133.6 * mm, "offsetDistance" : 30.48 * mm});
        }
        {
            var Q0;
            Q0=makeQuery(id+"F6.opExtrude","SWEPT_FACE",FACE,{"disambiguationData":[OSD([sQuery(id+"F0.wireOp",EDGE,"E60")])]});
            var sketch = newSketch(context, id + "F8", { "sketchPlane" : qUnion([Q0])});
            skLineSegment(sketch, "E96.0", {"start": v(12591.09, 4572) * mm, "end": v(12591.09, 0) * mm});
            skLineSegment(sketch, "E97.0", {"start": v(24325.89, 0) * mm, "end": v(12591.09, 0) * mm});
            skLineSegment(sketch, "E98.0", {"start": v(24325.89, 4572) * mm, "end": v(24325.89, 0) * mm});
            skLineSegment(sketch, "E99", {"start": v(14419.89, 0) * mm, "end": v(14419.89, 762) * mm});
            skLineSegment(sketch, "E100", {"start": v(14419.89, 762) * mm, "end": v(13962.69, 762) * mm});
            skArc(sketch, "E101", {"start": v(13962.69, 762) * mm, "mid": v(14096.6, 438.71) * mm, "end": v(14419.89, 304.8) * mm});
            skLineSegment(sketch, "E102", {"start": v(14343.69, 0) * mm, "end": v(14343.69, 311.2) * mm});
            skArc(sketch, "E103.0", {"start": v(13988.09, 762) * mm, "mid": v(14114.56, 456.67) * mm, "end": v(14419.89, 330.2) * mm});
            skSolve(sketch);
        }
        {
            var Q0;
            {var subQ4=sQuery(id+"F8.wireOp",EDGE,"E103.0");Q0=makeQuery(id+"F8.imprint","IMPRINT",FACE,{"disambiguationData":[TD([[makeQuery(id+"F8.imprint","IMPRINT",EDGE,{"derivedFrom":subQ4}),-1.0]])]});}
            var Q1;
            {var subQ3=sQuery(id+"F8.wireOp",EDGE,"E102");Q1=makeQuery(id+"F8.imprint","IMPRINT",FACE,{"disambiguationData":[TD([[makeQuery(id+"F8.imprint","IMPRINT",EDGE,{"derivedFrom":subQ3}),-1.0]])]});}
            var Q2;
            Q2=sQuery(id+"F8.wireOp",EDGE,"E99");
            revolve(context, id + "F9", {"operationType" : NewBodyOperationType.ADD, "surfaceOperationType" : NewSurfaceOperationType.NEW, "entities" : qUnion([Q0, Q1]), "axis" : qUnion([Q2]), "revolveType" : RevolveType.ONE_DIRECTION, "angle" : 180 * degree});
        }
        {
            var Q0;
            Q0=makeQuery(id+"F6.opExtrude","SWEPT_FACE",FACE,{"disambiguationData":[OSD([sQuery(id+"F0.wireOp",EDGE,"E1.top"),sQuery(id+"F0.wireOp",EDGE,"E2.top")])]});
            var sketch = newSketch(context, id + "F10", { "sketchPlane" : qUnion([Q0])});
            skLineSegment(sketch, "E104.0", {"start": v(-11430, 4572) * mm, "end": v(-228.6, 4572) * mm, "construction": true});
            skPoint(sketch, "E105", {"position": v(-5829.3, 4572) * mm});
            skLineSegment(sketch, "E106.bottom", {"start": v(-9906, 0) * mm, "end": v(-3810, 0) * mm});
            skLineSegment(sketch, "E106.top", {"start": v(-9906, 3657.6) * mm, "end": v(-3810, 3657.6) * mm});
            skLineSegment(sketch, "E106.left", {"start": v(-9906, 0) * mm, "end": v(-9906, 3657.6) * mm});
            skLineSegment(sketch, "E106.right", {"start": v(-3810, 0) * mm, "end": v(-3810, 3657.6) * mm});
            skSolve(sketch);
        }
        {
            var Q0;
            Q0=makeQuery(id+"F10.imprint","IMPRINT",FACE,{"disambiguationData":[TD([[makeQuery(id+"F10.imprint","IMPRINT",EDGE,{"derivedFrom":sQuery(id+"F10.wireOp",EDGE,"E106.bottom")}),1.0]])]});
            var Q1;
            Q1=makeQuery(id+"F6.opExtrude","SWEPT_FACE",FACE,{"disambiguationData":[OSD([sQuery(id+"F0.wireOp",EDGE,"E58.3")])]});
            extrude(context, id + "F11", {"entities" : qUnion([Q0]), "operationType" : NewBodyOperationType.REMOVE, "endBound" : BoundingType.UP_TO_SURFACE, "oppositeDirection" : true, "depth" : 822.96 * mm, "endBoundEntityFace" : qUnion([Q1]), "offsetDistance" : 30.48 * mm});
        }
    });
